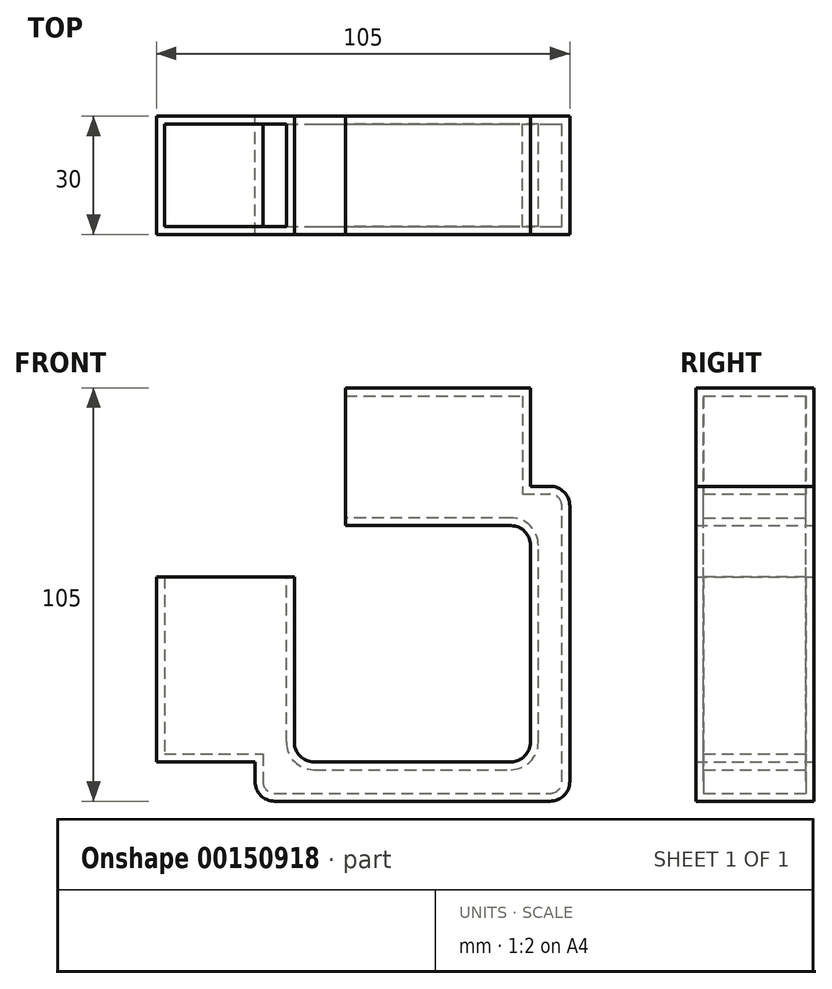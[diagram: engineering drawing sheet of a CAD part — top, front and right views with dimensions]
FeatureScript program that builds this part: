
annotation { "Feature Type Name" : "Feature", "Feature Type Description" : "" }
export const myFeature = defineFeature(function(context is Context, id is Id, definition is map)
    precondition{}
    {
        {
            var Q0;
            Q0=qCreatedBy(makeId("Front.planeOp"),FACE);
            var sketch = newSketch(context, id + "F0", { "sketchPlane" : qUnion([Q0])});
            skLineSegment(sketch, "E0", {"start": v(0, 5) * mm, "end": v(0, 47) * mm});
            skLineSegment(sketch, "E1", {"start": v(0, 47) * mm, "end": v(-35, 47) * mm});
            skLineSegment(sketch, "E2", {"start": v(-35, 47) * mm, "end": v(-35, 0) * mm});
            skLineSegment(sketch, "E3", {"start": v(-35, 0) * mm, "end": v(-10, 0) * mm});
            skLineSegment(sketch, "E4", {"start": v(-10, 0) * mm, "end": v(-10, -5) * mm});
            skLineSegment(sketch, "E5", {"start": v(-5, -10) * mm, "end": v(65, -10) * mm});
            skLineSegment(sketch, "E6", {"start": v(5, 0) * mm, "end": v(55, 0) * mm});
            skLineSegment(sketch, "E7", {"start": v(60, 5) * mm, "end": v(60, 55) * mm});
            skLineSegment(sketch, "E8", {"start": v(70, -5) * mm, "end": v(70, 65) * mm});
            skLineSegment(sketch, "E9", {"start": v(55, 60) * mm, "end": v(13, 60) * mm});
            skLineSegment(sketch, "E10", {"start": v(13, 60) * mm, "end": v(13, 95) * mm});
            skLineSegment(sketch, "E11", {"start": v(13, 95) * mm, "end": v(60, 95) * mm});
            skLineSegment(sketch, "E12", {"start": v(60, 95) * mm, "end": v(60, 70) * mm});
            skLineSegment(sketch, "E13", {"start": v(60, 70) * mm, "end": v(65, 70) * mm});
            skPoint(sketch, "E14.visualSharp", {"position": v(0, 0) * mm});
            skArc(sketch, "E14.filletArc", {"start": v(0, 5) * mm, "mid": v(1.46, 1.46) * mm, "end": v(5, 0) * mm});
            skPoint(sketch, "E15.visualSharp", {"position": v(60, 0) * mm});
            skArc(sketch, "E15.filletArc", {"start": v(55, 0) * mm, "mid": v(58.54, 1.46) * mm, "end": v(60, 5) * mm});
            skPoint(sketch, "E16.visualSharp", {"position": v(60, 60) * mm});
            skArc(sketch, "E16.filletArc", {"start": v(60, 55) * mm, "mid": v(58.54, 58.54) * mm, "end": v(55, 60) * mm});
            skPoint(sketch, "E17.visualSharp", {"position": v(70, 70) * mm});
            skArc(sketch, "E17.filletArc", {"start": v(70, 65) * mm, "mid": v(68.54, 68.54) * mm, "end": v(65, 70) * mm});
            skPoint(sketch, "E18.visualSharp", {"position": v(70, -10) * mm});
            skArc(sketch, "E18.filletArc", {"start": v(65, -10) * mm, "mid": v(68.54, -8.54) * mm, "end": v(70, -5) * mm});
            skPoint(sketch, "E19.visualSharp", {"position": v(-10, -10) * mm});
            skArc(sketch, "E19.filletArc", {"start": v(-10, -5) * mm, "mid": v(-8.54, -8.54) * mm, "end": v(-5, -10) * mm});
            skSolve(sketch);
        }
        {
            var Q0;
            Q0 = qSketchRegion(id + "F0", true);
            extrude(context, id + "F1", {"entities" : qUnion([Q0]), "depth" : 30 * mm});
        }
        {
            var Q0;
            Q0=makeQuery(id+"F1.opExtrude","SWEPT_FACE",FACE,{"disambiguationData":[OSD([sQuery(id+"F0.wireOp",EDGE,"E10")])]});
            shell(context, id + "F2", {"entities" : qUnion([Q0]), "thickness" : 2 * mm});
        }
        {
            var Q0;
            Q0=makeQuery(id+"F1.opExtrude","SWEPT_FACE",FACE,{"disambiguationData":[OSD([sQuery(id+"F0.wireOp",EDGE,"E1")])]});
            cPlane(context, id + "F3", {"entities" : qUnion([Q0]), "cplaneType" : CPlaneType.OFFSET, "offset" : 0 * mm, "width" : 150 * mm, "height" : 150 * mm});
        }
        {
            var Q0;
            Q0=qCreatedBy(id+"F3.planeOp",FACE);
            var sketch = newSketch(context, id + "F4", { "sketchPlane" : qUnion([Q0])});
            skLineSegment(sketch, "E20.bottom", {"start": v(-33, -2) * mm, "end": v(-2, -2) * mm});
            skLineSegment(sketch, "E20.top", {"start": v(-33, -28) * mm, "end": v(-2, -28) * mm});
            skLineSegment(sketch, "E20.left", {"start": v(-33, -2) * mm, "end": v(-33, -28) * mm});
            skLineSegment(sketch, "E20.right", {"start": v(-2, -2) * mm, "end": v(-2, -28) * mm});
            skSolve(sketch);
        }
        {
            var Q0;
            Q0 = qSketchRegion(id + "F4", true);
            extrude(context, id + "F5", {"entities" : qUnion([Q0]), "operationType" : NewBodyOperationType.REMOVE, "oppositeDirection" : true, "depth" : 4 * mm});
        }
    });
